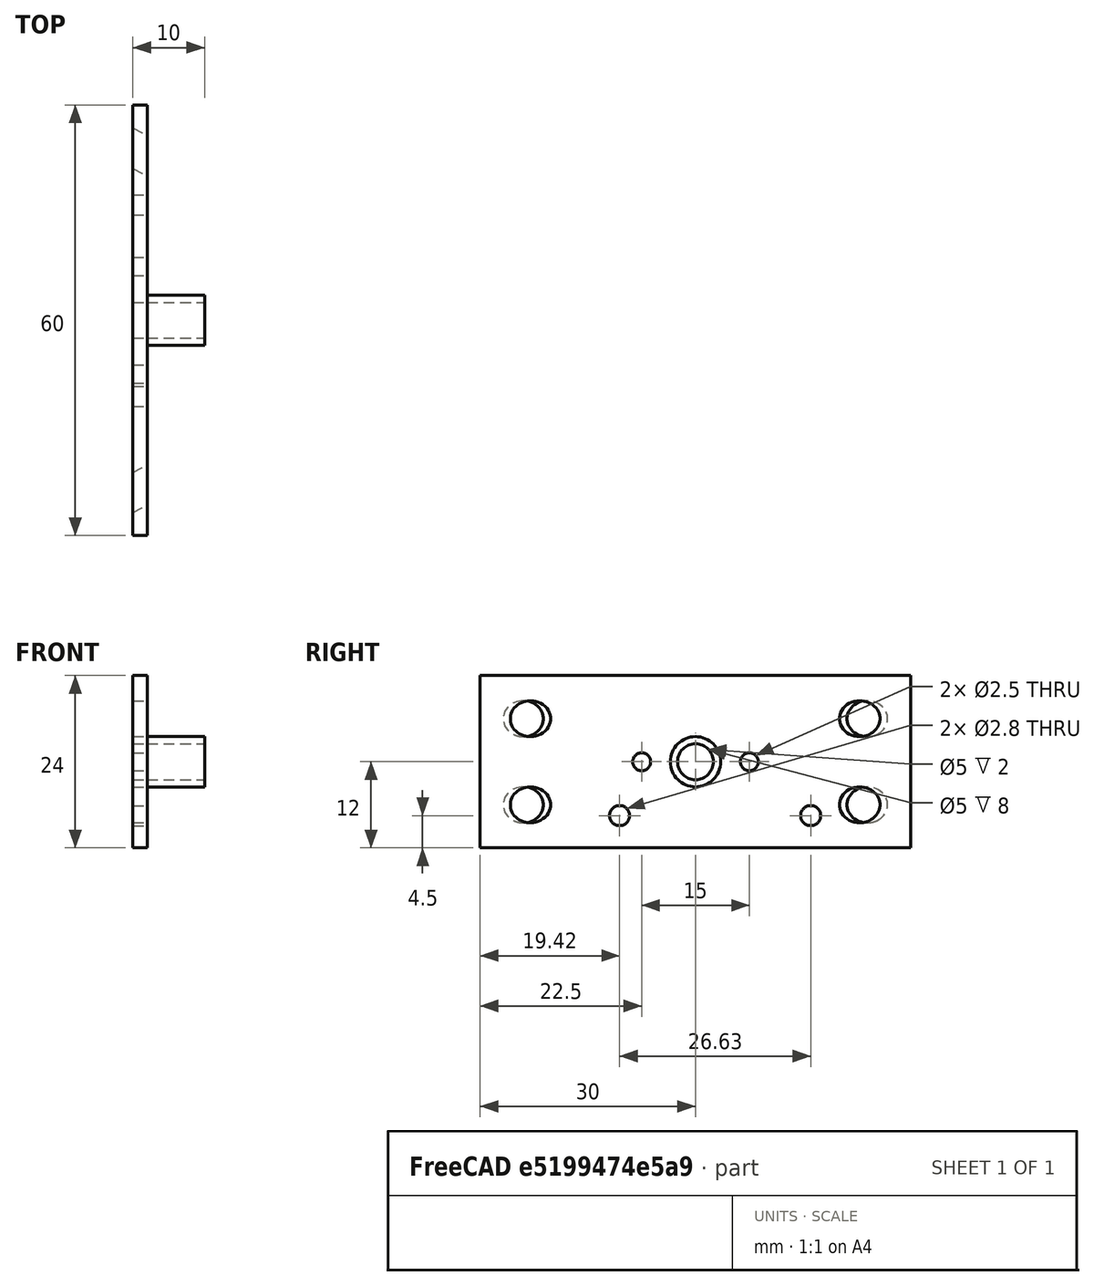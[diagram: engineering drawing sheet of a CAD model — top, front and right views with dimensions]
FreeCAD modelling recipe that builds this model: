
FCSTD DOCUMENT  (FreeCAD 0.15R4671 (Git))
Label: Frontblende_Loecher_Groß_Proto_Fertig2
License: All rights reserved
LicenseURL: http://en.wikipedia.org/wiki/All_rights_reserved
objects: Part::Cylinder×10, Part::Cut×10, Part::Box×1, Part::MultiFuse×1
note: 22 computed .brp shape members not serialized (recipe doc carries the construction recipe); baked Part::Feature solids carry a one-line shape summary decoded from their .brp

FEATURE [Part::Box] Box  label="Würfel"
  Height = 24
  Length = 2
  Width = 60
FEATURE [Part::Cylinder] Cylinder  label="Zylinder"
  Angle = 360
  Height = 10
  Placement = pos=(-2,5,6) rot=(-0.447214,0.894427,0;1.5708rad)
  Radius = 2.5
FEATURE [Part::Cylinder] Cylinder001  label="Zylinder001"
  Angle = 360
  Height = 10
  Placement = pos=(0,22.5,12) rot=(0,1,0;1.5708rad)
  Radius = 1.25
FEATURE [Part::Cylinder] Cylinder002  label="Zylinder002"
  Angle = 360
  Height = 10
  Placement = pos=(0,37.5,12) rot=(0,1,0;1.5708rad)
  Radius = 1.25
FEATURE [Part::Cylinder] Cylinder003  label="Zylinder003"
  Angle = 360
  Height = 10
  Placement = pos=(0,30,12) rot=(0,1,0;1.5708rad)
  Radius = 3.5
FEATURE [Part::Cylinder] Cylinder004  label="Zylinder004"
  Angle = 360
  Height = 12
  Placement = pos=(0,30,12) rot=(0,1,0;1.5708rad)
  Radius = 2.5
FEATURE [Part::Cylinder] Cylinder005  label="Zylinder005"
  Angle = 360
  Height = 10
  Placement = pos=(-2,5,18) rot=(-0.447214,0.894427,0;1.5708rad)
  Radius = 2.5
FEATURE [Part::Cylinder] Cylinder006  label="Zylinder006"
  Angle = 360
  Height = 10
  Placement = pos=(-2,55,18) rot=(0.467599,0.883941,0;1.5708rad)
  Radius = 2.5
FEATURE [Part::Cylinder] Cylinder007  label="Zylinder007"
  Angle = 360
  Height = 10
  Placement = pos=(-2,55,6) rot=(0.467599,0.883941,0;1.5708rad)
  Radius = 2.5
FEATURE [Part::Cut] Cut
  Base = -> Box
  Tool = -> Cylinder005
FEATURE [Part::Cut] Cut001
  Base = -> Cut
  Tool = -> Cylinder
FEATURE [Part::Cut] Cut002
  Base = -> Cut001
  Tool = -> Cylinder006
FEATURE [Part::Cut] Cut003
  Base = -> Cut002
  Tool = -> Cylinder007
FEATURE [Part::Cut] Cut004
  Base = -> Cut003
  Tool = -> Cylinder002
FEATURE [Part::Cut] Cut005
  Base = -> Cut004
  Tool = -> Cylinder001
FEATURE [Part::Cut] Cut006
  Base = -> Cylinder003
  Tool = -> Cylinder004
FEATURE [Part::Cut] Cut007
  Base = -> Cut005
  Tool = -> Cylinder004
FEATURE [Part::Cylinder] Cylinder008  label="Zylinder008"
  Angle = 360
  Height = 10
  Placement = pos=(-1,19.42,4.5) rot=(0,1,0;1.5708rad)
  Radius = 1.4
FEATURE [Part::Cylinder] Cylinder009  label="Zylinder009"
  Angle = 360
  Height = 10
  Placement = pos=(-1,46.05,4.5) rot=(0,1,0;1.5708rad)
  Radius = 1.4
FEATURE [Part::Cut] Cut008
  Base = -> Cut007
  Tool = -> Cylinder008
FEATURE [Part::Cut] Cut009
  Base = -> Cut008
  Tool = -> Cylinder009
FEATURE [Part::MultiFuse] Fusion
  Shapes = -> [Cut009,Cut006]
